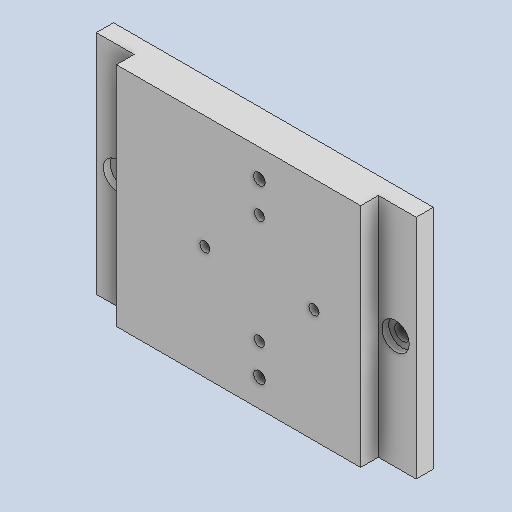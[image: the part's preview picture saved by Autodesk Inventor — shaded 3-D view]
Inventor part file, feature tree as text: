
AUTODESK INVENTOR PART (.ipt)
format: ipt  version: 2024.2 (Build 282272000, 272)  size: 152,576 bytes
history: native  units: in
note: dims shown in document units (in); Inventor stores cm internally (conversion verified against a paired STEP export)
features: hole x3, extrude x2, sketch x1
ambient origin geometry x8: Origin, YZ Plane, XZ Plane, XY Plane, X Axis, Y Axis, Z Axis, Center Point
bodies: Solid1 (feature_tree)
feature tree (6):
  extrude  "Extrusion1"  Depth=3.6654in
  extrude  "Extrusion2"  Depth=2.5984in
  hole  "Hole1"  [1 undecoded]
  hole  "Hole2"  [1 undecoded]
  hole  "Hole3"  [1 undecoded]
  sketch  "Sketch5"  dims[d2=0.4in d3=0.0in d4=3.6654in d5=2.5984in d6=0.1969in d7=0.0in d8=0.2362in d9=0.2362in d10=0.0in d11=0.0in d12=0.1772in d13=0.33in d14=0.315in d15=0.0787in d16=0.5635in d17=0.4843in d18=0.0in d19=0.9843in d20=1.9681in d21=1.1598in d22=1.1598in d23=0.1339in d24=0.33in d25=0.2559in d26=0.1181in d27=0.5635in d28=0.4843in d29=0.0in d32=0.2398in d33=0.0in d34=1.25in d35=0.116in d36=0.33in d37=0.2188in d38=0.112in d39=0.5635in d40=0.4843in d41=0.0in]
note: 3 required parameter values undecoded (feature->parameter linkage not recoverable at this tier; creation-order binding heuristic only, values carry confidence <= 0.55)
